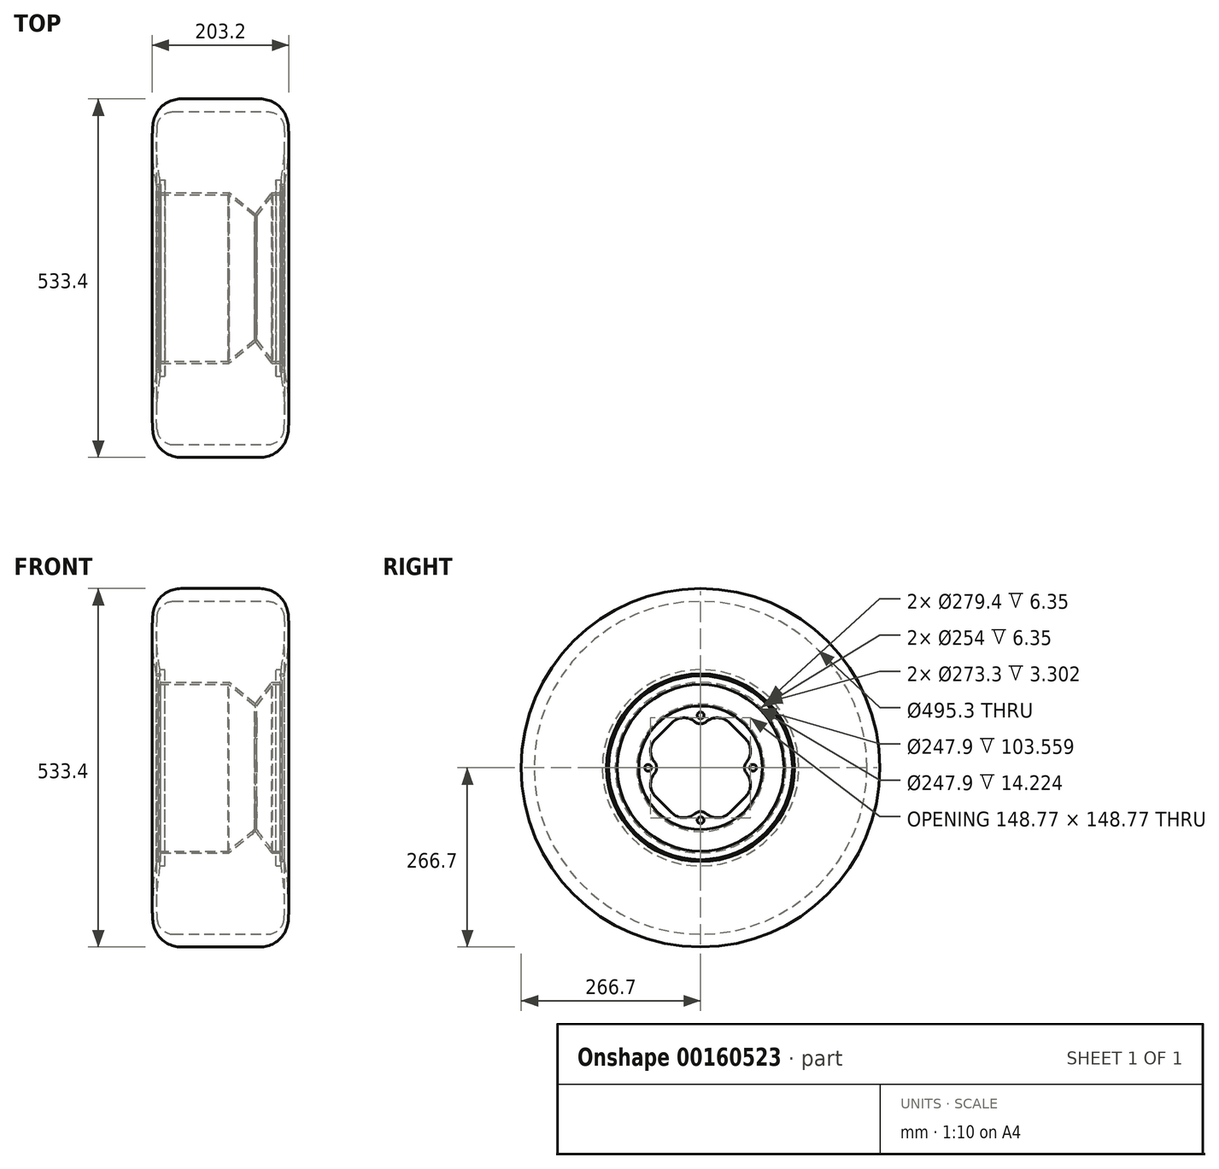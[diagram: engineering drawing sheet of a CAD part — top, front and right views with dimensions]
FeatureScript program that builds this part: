
annotation { "Feature Type Name" : "Feature", "Feature Type Description" : "" }
export const myFeature = defineFeature(function(context is Context, id is Id, definition is map)
    precondition{}
    {
        {
            var Q0;
            Q0=qCreatedBy(makeId("Front.planeOp"),FACE);
            var sketch = newSketch(context, id + "F0", { "sketchPlane" : qUnion([Q0])});
            skLineSegment(sketch, "E0", {"start": v(-141.1, 139.7) * mm, "end": v(-141.1, 127) * mm});
            skLineSegment(sketch, "E1", {"start": v(-141.1, 127) * mm, "end": v(-39.5, 127) * mm});
            skLineSegment(sketch, "E2", {"start": v(-39.5, 127) * mm, "end": v(-0.43, 95) * mm});
            skLineSegment(sketch, "E3", {"start": v(-0.43, 95) * mm, "end": v(0, 95) * mm});
            skLineSegment(sketch, "E4", {"start": v(0, 95) * mm, "end": v(24, 127) * mm});
            skLineSegment(sketch, "E5", {"start": v(24, 127) * mm, "end": v(36.7, 127) * mm});
            skLineSegment(sketch, "E6", {"start": v(36.7, 127) * mm, "end": v(36.7, 139.7) * mm});
            skLineSegment(sketch, "E7", {"start": v(36.7, 139.7) * mm, "end": v(43.05, 139.7) * mm});
            skLineSegment(sketch, "E8", {"start": v(43.05, 139.7) * mm, "end": v(43.05, 136.65) * mm});
            skLineSegment(sketch, "E9", {"start": v(43.05, 136.65) * mm, "end": v(39.75, 136.65) * mm});
            skLineSegment(sketch, "E10", {"start": v(39.75, 136.65) * mm, "end": v(39.75, 123.95) * mm});
            skLineSegment(sketch, "E11", {"start": v(39.75, 123.95) * mm, "end": v(25.53, 123.95) * mm});
            skLineSegment(sketch, "E12", {"start": v(25.53, 123.95) * mm, "end": v(1.52, 91.95) * mm});
            skLineSegment(sketch, "E13", {"start": v(1.52, 91.95) * mm, "end": v(1.52, 0) * mm});
            skLineSegment(sketch, "E14", {"start": v(-144.14, 136.65) * mm, "end": v(-144.14, 123.95) * mm});
            skLineSegment(sketch, "E15", {"start": v(-144.14, 123.95) * mm, "end": v(-40.59, 123.95) * mm});
            skLineSegment(sketch, "E16", {"start": v(-40.59, 123.95) * mm, "end": v(-1.52, 91.95) * mm});
            skLineSegment(sketch, "E17", {"start": v(-1.52, 91.95) * mm, "end": v(-1.52, 0) * mm});
            skLineSegment(sketch, "E18.top", {"start": v(-144.14, 136.65) * mm, "end": v(-147.45, 136.65) * mm});
            skLineSegment(sketch, "E18.right", {"start": v(-147.45, 139.7) * mm, "end": v(-147.45, 136.65) * mm});
            skLineSegment(sketch, "E19", {"start": v(-141.1, 139.7) * mm, "end": v(-147.45, 139.7) * mm});
            skLineSegment(sketch, "E20", {"start": v(1.52, 0) * mm, "end": v(-1.52, 0) * mm});
            skLineSegment(sketch, "E21", {"start": v(159.98, 0) * mm, "end": v(-159.98, 0) * mm, "construction": true});
            skSolve(sketch);
        }
        {
            var Q0;
            Q0 = qSketchRegion(id + "F0", true);
            var Q1;
            Q1=sQuery(id+"F0.wireOp",EDGE,"E21");
            revolve(context, id + "F1", {"entities" : qUnion([Q0]), "axis" : qUnion([Q1]), "revolveType" : RevolveType.FULL});
        }
        {
            var Q0;
            Q0=qCreatedBy(makeId("Front.planeOp"),FACE);
            var sketch = newSketch(context, id + "F2", { "sketchPlane" : qUnion([Q0])});
            skPoint(sketch, "E22", {"position": v(-52.2, 0) * mm});
            skLineSegment(sketch, "E23", {"start": v(-52.2, 0) * mm, "end": v(-52.2, 266.7) * mm, "construction": true});
            skLineSegment(sketch, "E24.MirrorCS", {"start": v(-141.1, 127) * mm, "end": v(-141.1, 139.7) * mm});
            skLineSegment(sketch, "E25.MirrorCS", {"start": v(-141.1, 139.7) * mm, "end": v(-147.45, 139.7) * mm});
            skLineSegment(sketch, "E26.MirrorCS", {"start": v(-175.42, 247.65) * mm, "end": v(-175.42, 247.65) * mm});
            skLineSegment(sketch, "E27.MirrorCS", {"start": v(-52.2, 266.7) * mm, "end": v(-110.86, 266.7) * mm});
            skArc(sketch, "E28.MirrorCS", {"start": v(-152.81, 227.92) * mm, "mid": v(-139.42, 255.52) * mm, "end": v(-110.86, 266.7) * mm});
            skArc(sketch, "E29.MirrorCS", {"start": v(-147.45, 139.7) * mm, "mid": v(-153.21, 183.62) * mm, "end": v(-152.81, 227.92) * mm});
            skLineSegment(sketch, "E30", {"start": v(43.05, 0) * mm, "end": v(-147.45, 0) * mm, "construction": true});
            skLineSegment(sketch, "E31.0", {"start": v(-51.38, 247.65) * mm, "end": v(-122.23, 247.65) * mm});
            skLineSegment(sketch, "E31.1", {"start": v(-134.75, 127) * mm, "end": v(-134.75, 146.05) * mm});
            skLineSegment(sketch, "E31.2", {"start": v(-134.75, 146.05) * mm, "end": v(-142.21, 146.05) * mm});
            skArc(sketch, "E31.3", {"start": v(-142.21, 146.05) * mm, "mid": v(-146.95, 185.32) * mm, "end": v(-146.67, 224.87) * mm});
            skLineSegment(sketch, "E32", {"start": v(-134.75, 127) * mm, "end": v(-141.1, 127) * mm});
            skLineSegment(sketch, "E33.MirrorCS", {"start": v(36.7, 139.7) * mm, "end": v(43.05, 139.7) * mm});
            skLineSegment(sketch, "E34.MirrorCS", {"start": v(36.7, 127) * mm, "end": v(36.7, 139.7) * mm});
            skLineSegment(sketch, "E35.MirrorCS", {"start": v(30.35, 127) * mm, "end": v(36.7, 127) * mm});
            skLineSegment(sketch, "E36.MirrorCS", {"start": v(30.35, 146.05) * mm, "end": v(37.82, 146.05) * mm});
            skLineSegment(sketch, "E37.MirrorCS", {"start": v(-52.2, 266.7) * mm, "end": v(6.46, 266.7) * mm});
            skLineSegment(sketch, "E38.MirrorCS", {"start": v(30.35, 127) * mm, "end": v(30.35, 146.05) * mm});
            skLineSegment(sketch, "E39.MirrorCS", {"start": v(-53, 247.65) * mm, "end": v(17.83, 247.65) * mm});
            skArc(sketch, "E40.MirrorCS", {"start": v(37.82, 146.05) * mm, "mid": v(42.56, 185.32) * mm, "end": v(42.28, 224.87) * mm});
            skArc(sketch, "E41.MirrorCS", {"start": v(48.42, 227.92) * mm, "mid": v(35.03, 255.52) * mm, "end": v(6.46, 266.7) * mm});
            skArc(sketch, "E42.MirrorCS", {"start": v(43.05, 139.7) * mm, "mid": v(48.82, 183.62) * mm, "end": v(48.42, 227.92) * mm});
            skArc(sketch, "E43", {"start": v(-122.23, 247.65) * mm, "mid": v(-138.94, 241.07) * mm, "end": v(-146.67, 224.87) * mm});
            skArc(sketch, "E44", {"start": v(17.83, 247.65) * mm, "mid": v(34.54, 241.07) * mm, "end": v(42.28, 224.87) * mm});
            skSolve(sketch);
        }
        {
            var Q0;
            Q0=makeQuery(id+"F1.opRevolve","SWEPT_FACE",FACE,{"disambiguationData":[OSD([sQuery(id+"F0.wireOp",EDGE,"E13")])]});
            var sketch = newSketch(context, id + "F3", { "sketchPlane" : qUnion([Q0])});
            skCircle(sketch, "E45", {"center": v(0, 78) * mm, "radius": 5 * mm});
            skArc(sketch, "E46", {"start": v(0, 65.3) * mm, "mid": v(4.39, 66.08) * mm, "end": v(8.24, 68.33) * mm});
            skLineSegment(sketch, "E47", {"start": v(0, 0) * mm, "end": v(78, 0) * mm, "construction": true});
            skLineSegment(sketch, "E48", {"start": v(0, 78) * mm, "end": v(0, 0) * mm, "construction": true});
            skArc(sketch, "E49", {"start": v(8.24, 68.33) * mm, "mid": v(25.72, 74.38) * mm, "end": v(42.68, 66.96) * mm});
            skLineSegment(sketch, "E50", {"start": v(42.68, 66.96) * mm, "end": v(66.96, 42.68) * mm});
            skArc(sketch, "E51", {"start": v(66.96, 42.68) * mm, "mid": v(74.38, 25.72) * mm, "end": v(68.33, 8.24) * mm});
            skArc(sketch, "E52", {"start": v(68.33, 8.24) * mm, "mid": v(66.08, 4.39) * mm, "end": v(65.3, 0) * mm});
            skLineSegment(sketch, "E53.1.0", {"start": v(-66.96, 42.68) * mm, "end": v(-42.68, 66.96) * mm});
            skArc(sketch, "E53.1.1", {"start": v(-42.68, 66.96) * mm, "mid": v(-25.72, 74.38) * mm, "end": v(-8.24, 68.33) * mm});
            skArc(sketch, "E53.1.2", {"start": v(-68.33, 8.24) * mm, "mid": v(-74.38, 25.72) * mm, "end": v(-66.96, 42.68) * mm});
            skArc(sketch, "E53.1.3", {"start": v(-65.3, 0) * mm, "mid": v(-66.08, 4.39) * mm, "end": v(-68.33, 8.24) * mm});
            skCircle(sketch, "E53.1.4", {"center": v(-78, 0) * mm, "radius": 5 * mm});
            skArc(sketch, "E53.1.5", {"start": v(-8.24, 68.33) * mm, "mid": v(-4.39, 66.08) * mm, "end": v(0, 65.3) * mm});
            skLineSegment(sketch, "E53.2.0", {"start": v(-42.68, -66.96) * mm, "end": v(-66.96, -42.68) * mm});
            skArc(sketch, "E53.2.1", {"start": v(-66.96, -42.68) * mm, "mid": v(-74.38, -25.72) * mm, "end": v(-68.33, -8.24) * mm});
            skArc(sketch, "E53.2.2", {"start": v(-8.24, -68.33) * mm, "mid": v(-25.72, -74.38) * mm, "end": v(-42.68, -66.96) * mm});
            skArc(sketch, "E53.2.3", {"start": v(0, -65.3) * mm, "mid": v(-4.39, -66.08) * mm, "end": v(-8.24, -68.33) * mm});
            skCircle(sketch, "E53.2.4", {"center": v(0, -78) * mm, "radius": 5 * mm});
            skArc(sketch, "E53.2.5", {"start": v(-68.33, -8.24) * mm, "mid": v(-66.08, -4.39) * mm, "end": v(-65.3, 0) * mm});
            skLineSegment(sketch, "E53.3.0", {"start": v(66.96, -42.68) * mm, "end": v(42.68, -66.96) * mm});
            skArc(sketch, "E53.3.1", {"start": v(42.68, -66.96) * mm, "mid": v(25.72, -74.38) * mm, "end": v(8.24, -68.33) * mm});
            skArc(sketch, "E53.3.2", {"start": v(68.33, -8.24) * mm, "mid": v(74.38, -25.72) * mm, "end": v(66.96, -42.68) * mm});
            skArc(sketch, "E53.3.3", {"start": v(65.3, 0) * mm, "mid": v(66.08, -4.39) * mm, "end": v(68.33, -8.24) * mm});
            skCircle(sketch, "E53.3.4", {"center": v(78, 0) * mm, "radius": 5 * mm});
            skArc(sketch, "E53.3.5", {"start": v(8.24, -68.33) * mm, "mid": v(4.39, -66.08) * mm, "end": v(0, -65.3) * mm});
            skPoint(sketch, "E53.center", {"position": v(0, 0) * mm});
            skSolve(sketch);
        }
        {
            var Q0;
            Q0=qSketchRegion(id+"F3",true);
            extrude(context, id + "F4", {"entities" : qUnion([Q0]), "operationType" : NewBodyOperationType.REMOVE, "endBound" : BoundingType.THROUGH_ALL, "oppositeDirection" : true, "depth" : 25.4 * mm});
        }
        {
            var Q0;
            Q0=qSketchRegion(id+"F2",true);
            var Q1;
            Q1=sQuery(id+"F2.wireOp",EDGE,"E30");
            revolve(context, id + "F5", {"entities" : qUnion([Q0]), "axis" : qUnion([Q1]), "revolveType" : RevolveType.FULL});
        }
    });
